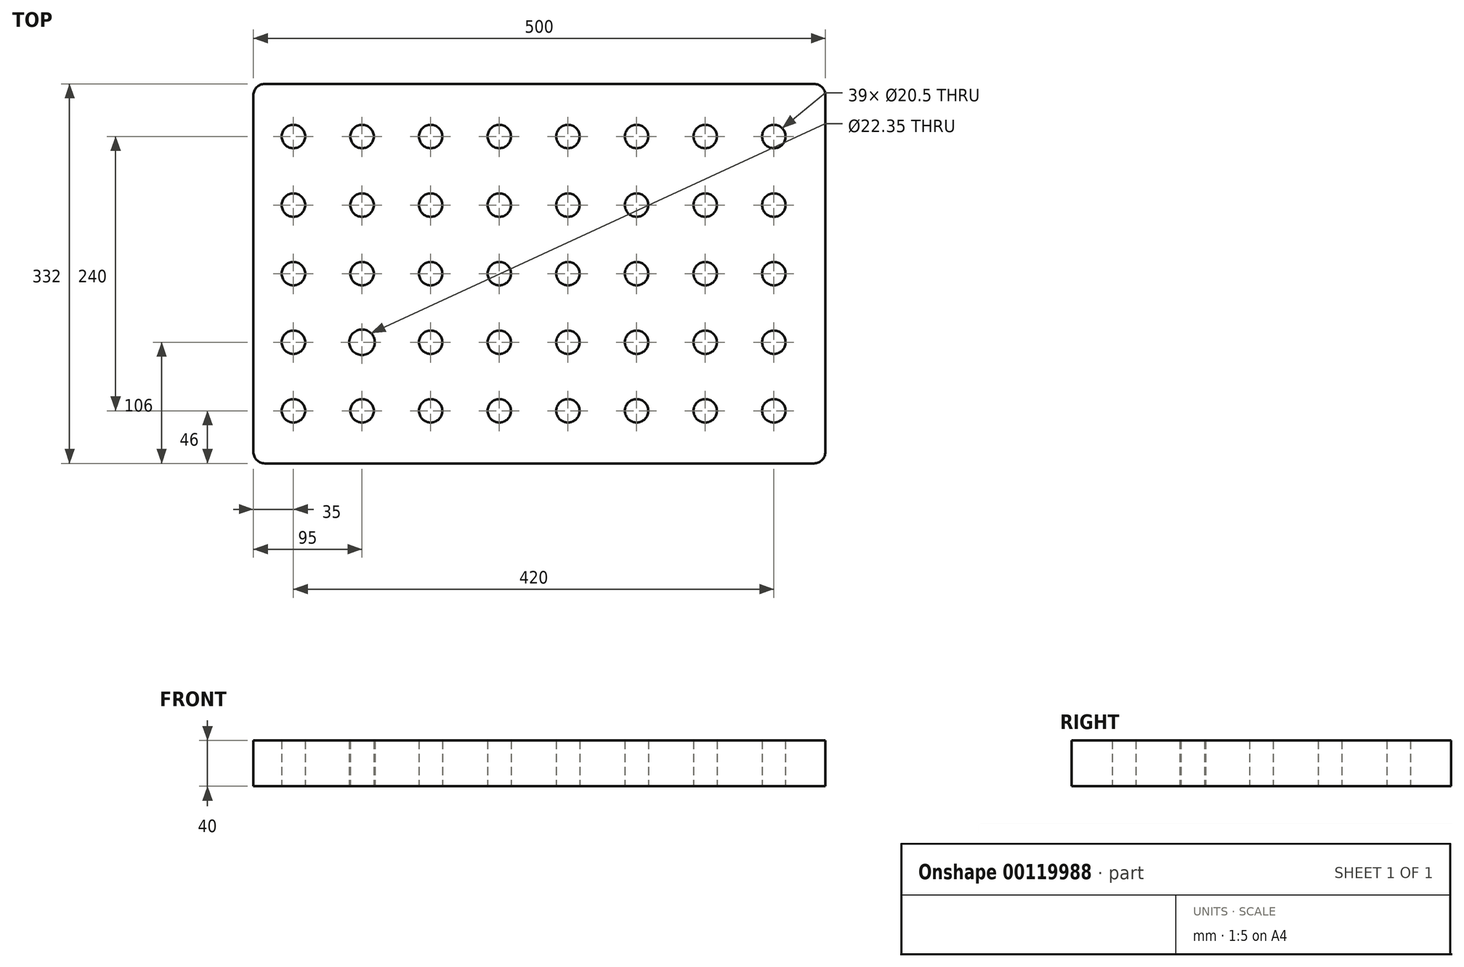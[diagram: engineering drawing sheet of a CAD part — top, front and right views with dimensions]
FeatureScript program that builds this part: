
annotation { "Feature Type Name" : "Feature", "Feature Type Description" : "" }
export const myFeature = defineFeature(function(context is Context, id is Id, definition is map)
    precondition{}
    {
        {
            var Q0;
            Q0=qCreatedBy(makeId("Top.planeOp"),FACE);
            var sketch = newSketch(context, id + "F0", { "sketchPlane" : qUnion([Q0])});
            skLineSegment(sketch, "E0.bottom", {"start": v(240, -166) * mm, "end": v(-240, -166) * mm});
            skLineSegment(sketch, "E0.top", {"start": v(240, 166) * mm, "end": v(-240, 166) * mm});
            skLineSegment(sketch, "E0.left", {"start": v(250, -156) * mm, "end": v(250, 156) * mm});
            skLineSegment(sketch, "E0.right", {"start": v(-250, -156) * mm, "end": v(-250, 156) * mm});
            skPoint(sketch, "E0.middle", {"position": v(0, 0) * mm});
            skCircle(sketch, "E1", {"center": v(-215, -120) * mm, "radius": 10.25 * mm});
            skCircle(sketch, "E2", {"center": v(-215, -60) * mm, "radius": 10.25 * mm});
            skCircle(sketch, "E3", {"center": v(-215, 0) * mm, "radius": 10.25 * mm});
            skCircle(sketch, "E4", {"center": v(-215, 60) * mm, "radius": 10.25 * mm});
            skCircle(sketch, "E5", {"center": v(-215, 120) * mm, "radius": 10.25 * mm});
            skCircle(sketch, "E6", {"center": v(-155, -120) * mm, "radius": 10.25 * mm});
            skCircle(sketch, "E7", {"center": v(-155, -60) * mm, "radius": 11.17 * mm});
            skCircle(sketch, "E8", {"center": v(-155, 0) * mm, "radius": 10.25 * mm});
            skCircle(sketch, "E9", {"center": v(-155, 60) * mm, "radius": 10.25 * mm});
            skCircle(sketch, "E10", {"center": v(-155, 120) * mm, "radius": 10.25 * mm});
            skCircle(sketch, "E11", {"center": v(-95, -120) * mm, "radius": 10.25 * mm});
            skCircle(sketch, "E12", {"center": v(-35, -120) * mm, "radius": 10.25 * mm});
            skCircle(sketch, "E13", {"center": v(-95, -60) * mm, "radius": 10.25 * mm});
            skCircle(sketch, "E14", {"center": v(-35, -60) * mm, "radius": 10.25 * mm});
            skCircle(sketch, "E15", {"center": v(-95, 0) * mm, "radius": 10.25 * mm});
            skCircle(sketch, "E16", {"center": v(-35, 0) * mm, "radius": 10.25 * mm});
            skCircle(sketch, "E17", {"center": v(-95, 60) * mm, "radius": 10.25 * mm});
            skCircle(sketch, "E18", {"center": v(-35, 60) * mm, "radius": 10.25 * mm});
            skCircle(sketch, "E19", {"center": v(-95, 120) * mm, "radius": 10.25 * mm});
            skCircle(sketch, "E20", {"center": v(-35, 120) * mm, "radius": 10.25 * mm});
            skCircle(sketch, "E21", {"center": v(25, -120) * mm, "radius": 10.25 * mm});
            skCircle(sketch, "E22", {"center": v(85, -120) * mm, "radius": 10.25 * mm});
            skCircle(sketch, "E23", {"center": v(25, -60) * mm, "radius": 10.25 * mm});
            skCircle(sketch, "E24", {"center": v(85, -60) * mm, "radius": 10.25 * mm});
            skCircle(sketch, "E25", {"center": v(25, 0) * mm, "radius": 10.25 * mm});
            skCircle(sketch, "E26", {"center": v(85, 0) * mm, "radius": 10.25 * mm});
            skCircle(sketch, "E27", {"center": v(25, 60) * mm, "radius": 10.25 * mm});
            skCircle(sketch, "E28", {"center": v(85, 60) * mm, "radius": 10.25 * mm});
            skCircle(sketch, "E29", {"center": v(25, 120) * mm, "radius": 10.25 * mm});
            skCircle(sketch, "E30", {"center": v(85, 120) * mm, "radius": 10.25 * mm});
            skCircle(sketch, "E31.MirrorC", {"center": v(145, -120) * mm, "radius": 10.25 * mm});
            skCircle(sketch, "E32.MirrorC", {"center": v(145, 60) * mm, "radius": 10.25 * mm});
            skCircle(sketch, "E33.MirrorC", {"center": v(145, 120) * mm, "radius": 10.25 * mm});
            skCircle(sketch, "E34.MirrorC", {"center": v(205, -120) * mm, "radius": 10.25 * mm});
            skCircle(sketch, "E35.MirrorC", {"center": v(205, 0) * mm, "radius": 10.25 * mm});
            skCircle(sketch, "E36.MirrorC", {"center": v(205, -60) * mm, "radius": 10.25 * mm});
            skCircle(sketch, "E37.MirrorC", {"center": v(205, 60) * mm, "radius": 10.25 * mm});
            skCircle(sketch, "E38.MirrorC", {"center": v(205, 120) * mm, "radius": 10.25 * mm});
            skCircle(sketch, "E39.MirrorC", {"center": v(145, -60) * mm, "radius": 10.25 * mm});
            skCircle(sketch, "E40.MirrorC", {"center": v(145, 0) * mm, "radius": 10.25 * mm});
            skPoint(sketch, "E41.visualSharp", {"position": v(-250, 166) * mm});
            skArc(sketch, "E41.filletArc", {"start": v(-240, 166) * mm, "mid": v(-247.07, 163.07) * mm, "end": v(-250, 156) * mm});
            skPoint(sketch, "E42.visualSharp", {"position": v(250, 166) * mm});
            skArc(sketch, "E42.filletArc", {"start": v(250, 156) * mm, "mid": v(247.07, 163.07) * mm, "end": v(240, 166) * mm});
            skPoint(sketch, "E43.visualSharp", {"position": v(250, -166) * mm});
            skArc(sketch, "E43.filletArc", {"start": v(240, -166) * mm, "mid": v(247.07, -163.07) * mm, "end": v(250, -156) * mm});
            skPoint(sketch, "E44.visualSharp", {"position": v(-250, -166) * mm});
            skArc(sketch, "E44.filletArc", {"start": v(-250, -156) * mm, "mid": v(-247.07, -163.07) * mm, "end": v(-240, -166) * mm});
            skSolve(sketch);
        }
        {
            var Q0;
            Q0 = qSketchRegion(id + "F0", true);
            extrude(context, id + "F1", {"entities" : qUnion([Q0]), "depth" : 40 * mm});
        }
    });
